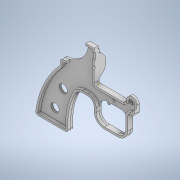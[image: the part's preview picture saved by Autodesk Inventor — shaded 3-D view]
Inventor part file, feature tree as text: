
AUTODESK INVENTOR PART (.ipt)
format: ipt  version: 2021 (Build 250183000, 183)  size: 440,832 bytes
history: native  units: in
note: dims shown in document units (in); Inventor stores cm internally (conversion verified against a paired STEP export)
features: sketch x14, extrude x10, fillet x1, chamfer x1, plane x1, revolve x1
ambient origin geometry x8: Origin, YZ Plane, XZ Plane, XY Plane, X Axis, Y Axis, Z Axis, Center Point
bodies: Solid1 (feature_tree)
feature tree (28):
  extrude  "Extrusion1"  Depth=1.3189in
  extrude  "Extrusion2"  Depth=0.1181in
  extrude  "Extrusion3"  Depth=0.1181in
  extrude  "Extrusion4"  Depth=0.1181in
  sketch  "Sketch5"  dims[d10=0.1181in d11=1.3112in]
  extrude  "Extrusion5"  Depth=0.1181in
  extrude  "Extrusion6"  Depth=0.3937in
  extrude  "Extrusion7"  Depth=0.3937in
  extrude  "Extrusion8"  Depth=0.2953in
  fillet  "Fillet1"  Radius=0.1969in
  chamfer  "Chamfer2"  Distance=0.315in
  sketch  "Sketch11"  dims[d20=0.6299in]
  sketch  "Sketch12"  dims[d21=0.4921in]
  plane  "Work Plane1"
  revolve  "Revolution1"  [1 undecoded]
  extrude  "Extrusion9"  Depth=0.1378in
  extrude  "Extrusion10"  Depth=0.0394in
  sketch  "Sketch1"  dims[d2=0.4015in d3=1.3189in]
  sketch  "Sketch2"  dims[d4=1.2205in d5=0.1181in]
  sketch  "Sketch3"  dims[d6=0.1344in d7=0.1181in]
  sketch  "Sketch4"  dims[d8=4.5276in d9=0.1181in]
  sketch  "Sketch6"  dims[d12=0.3937in d13=0.3937in]
  sketch  "Sketch7"  dims[d14=2.9528in d15=0.3937in]
  sketch  "Sketch8"  dims[d16=0.2611in d17=0.2953in d18=0.1969in]
  sketch  "Sketch9"  dims[d19=0.4921in]
  sketch  "Sketch14"  dims[d22=0.6102in]
  sketch  "Sketch15"  dims[d23=0.1181in]
  sketch  "Sketch17"  dims[d25=0.1181in d26=0.315in d27=0.2362in d28=0.1378in d29=0.0394in d30=1.3386in d33=0.0394in d35=0.0394in d36=0.0787in d37=0.0787in d38=0.0787in d39=1.105in d40=1.0779in d41=0.1176in d42=0.1077in d43=0.031in d44=0.0798in d45=0.4724in d46=0.0787in d47=0.2362in d48=0.1181in d49=0.1181in d52=0.1181in d53=0.1181in d57=0.1181in d58=0.1181in d59=0.0787in d60=0.1969in d61=1.0827in d62=0.4921in d63=0.4921in d64=0.4921in d65=0.4921in d66=1.4173in d67=0.1969in d68=0.1969in d69=0.6299in d70=0.6299in d71=0.3937in d72=0.3937in d73=0.8858in d74=0.9843in d75=0.0984in d76=0.0in d77=0.1378in d78=0.0in d79=0.0394in d80=0.0in d81=0.0984in d82=0.0in d83=0.0591in d84=0.0in d85=0.0787in d86=0.0in d87=0.1378in d88=0.0in d89=0.1378in d90=0.0in d91=0.0162in d96=0.0787in d97=0.0787in d98=45.0deg d110=0.2482in d111=90.0deg d115=0.0262in d116=0.3346in d117=0.2482in d118=0.7087in d119=180.0deg d120=0.2482in d121=90.0deg d122=0.0262in d123=0.3346in d124=0.2482in d125=0.7087in d126=1.9685in d127=0.0in d134=0.0262in d135=0.0in d93=0.0197in d94=0.0344in d95=0.0197in]
note: 1 required parameter value undecoded (feature->parameter linkage not recoverable at this tier; creation-order binding heuristic only, values carry confidence <= 0.55)
